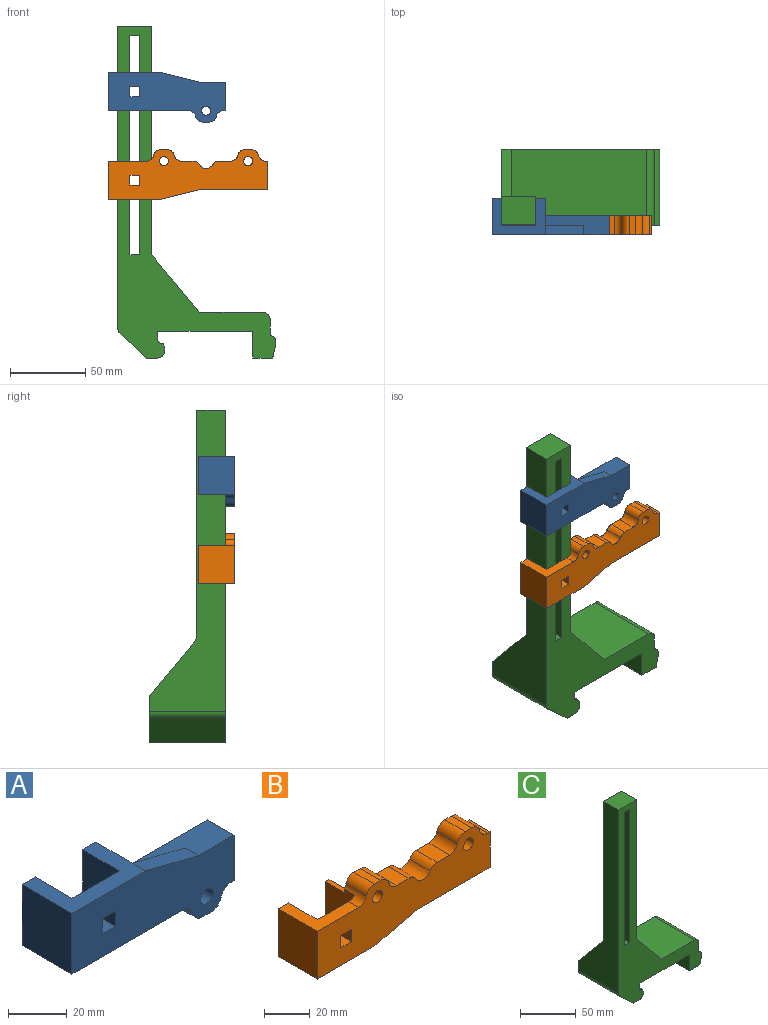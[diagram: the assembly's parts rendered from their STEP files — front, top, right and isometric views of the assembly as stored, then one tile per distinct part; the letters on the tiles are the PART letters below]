
ASSEMBLY  parts=3 mates=2
PART A: 33 faces, bbox 78.2x24.1x33 mm
  f0: plane 25.4x24.13mm, normal (-1,0,0), area 612.9mm2, adj f1,f2,f5,f32
  f1: plane 35.56x24.13mm, normal (0,0,1), area 451.6mm2, adj f0,f5,f6,f7,f8,f9,f16,f31
  f2: plane 53.5x24.13mm, normal (0,0,-1), area 679.4mm2, adj f0,f3,f5,f6,f7,f8,f9,f30
  f3: plane 42.65x26.67mm, normal (0,1,0), area 830.4mm2, adj f2,f4,f9,f14,f15,f18,f19,f20
  f4: plane 12.7x1.29mm, normal (0,0,-1), area 16.3mm2, adj f3,f5,f14,f29
  f5: plane 78.21x33.02mm, normal (0,-1,0), area 1829.8mm2, adj f0,f1,f2,f4,f10,f11,f12,f13
  f6: plane 25.4x22.86mm, normal (0,1,0), area 538.4mm2, adj f1,f2,f7,f8,f10,f11,f12,f13
  f7: plane 25.4x17.78mm, normal (-1,0,0), area 451.6mm2, adj f1,f2,f6,f31
  f8: plane 25.4x17.78mm, normal (1,0,0), area 451.6mm2, adj f1,f2,f6,f32
  f9: plane 25.4x17.78mm, normal (1,0,0), area 330.6mm2, adj f1,f2,f3,f15,f17,f31
  f10: plane 6.5x6.35mm, normal (0,0,1), area 41.3mm2, adj f5,f6,f11,f13
  f11: plane 6.5x6.35mm, normal (-1,0,0), area 41.3mm2, adj f5,f6,f10,f12
  f12: plane 6.5x6.35mm, normal (0,0,-1), area 41.3mm2, adj f5,f6,f11,f13
  f13: plane 6.5x6.35mm, normal (1,0,0), area 41.3mm2, adj f5,f6,f10,f12
  f14: plane 19.05x12.7mm, normal (1,0,0), area 241.9mm2, adj f3,f4,f5,f15
  f15: plane 42.65x12.7mm, normal (0,0,1), area 380.4mm2, adj f3,f5,f9,f14,f16,f17
  f16: plane 25.4x6.35mm, normal (0.24,0,0.97), area 166.3mm2, adj f1,f5,f15,f17
  f17: plane 25.4x6.35mm, normal (0,1,0), area 80.6mm2, adj f9,f15,f16
  f18: plane 12.7x4mm, normal (0,0,-1), area 50.8mm2, adj f3,f5,f19,f20
  f19: cylinder r=5mm len=12.7mm, axis (0,1,0), area 84.5mm2, adj f3,f5,f18,f29
  f20: cylinder r=5mm len=12.7mm, axis (0,-1,0), area 84.5mm2, adj f3,f5,f18,f30
  f21: cylinder r=3.02mm len=8.7mm, axis (0,1,0), area 165.4mm2, adj f5,f28
  f22: plane 5x4mm, normal (0.87,0,0.5), area 23.1mm2, adj f3,f23,f27,f28
  f23: plane 5x4mm, normal (0.87,0,-0.5), area 23.1mm2, adj f3,f22,f24,f28
  f24: plane 5.77x4mm, normal (0,0,-1), area 23.1mm2, adj f3,f23,f25,f28
  f25: plane 5x4mm, normal (-0.87,0,-0.5), area 23.1mm2, adj f3,f24,f26,f28
  f26: plane 5x4mm, normal (-0.87,0,0.5), area 23.1mm2, adj f3,f25,f27,f28
  f27: plane 5.77x4mm, normal (0,0,1), area 23.1mm2, adj f3,f22,f26,f28
  f28: plane 11.55x10mm, normal (0,1,0), area 57.9mm2, adj f21,f22,f23,f24,f25,f26,f27
  f29: cylinder r=5mm len=12.7mm, axis (0,1,0), area 84.5mm2, adj f3,f4,f5,f19
  f30: cylinder r=5mm len=12.7mm, axis (0,-1,0), area 84.5mm2, adj f2,f3,f5,f20
  f31: plane 25.4x6.35mm, normal (0,1,0), area 161.3mm2, adj f1,f2,f7,f9
  f32: plane 25.4x6.35mm, normal (0,1,0), area 161.3mm2, adj f0,f1,f2,f8
PART B: 59 faces, bbox 106.4x24.1x33 mm
  f0: plane 25.4x6.35mm, normal (0,1,0), area 147.5mm2, adj f2,f3,f18,f23,f56,f57
  f1: plane 77.2x26.67mm, normal (0,1,0), area 1352.3mm2, adj f2,f3,f13,f14,f15,f18,f22,f28
  f2: plane 11.43x2.17mm, normal (0,0,1), area 24.8mm2, adj f0,f1,f18,f57
  f3: plane 20.35x17.78mm, normal (1,0,0), area 272.9mm2, adj f0,f1,f15,f23,f30,f56
  f4: plane 5x3.43mm, normal (0.87,0,0.5), area 19.8mm2, adj f5,f9,f40,f58
  f5: plane 5x3.43mm, normal (0.87,0,-0.5), area 19.8mm2, adj f4,f6,f40,f58
  f6: plane 5.77x3.43mm, normal (0,0,-1), area 19.8mm2, adj f5,f7,f40,f58
  f7: plane 5x3.43mm, normal (-0.87,0,-0.5), area 19.8mm2, adj f6,f8,f40,f58
  f8: plane 5x3.43mm, normal (-0.87,0,0.5), area 19.8mm2, adj f7,f9,f40,f58
  f9: plane 5.77x3.43mm, normal (0,0,1), area 19.8mm2, adj f4,f8,f40,f58
  f10: plane 25.5x24.13mm, normal (0,0,1), area 274.8mm2, adj f16,f17,f19,f20,f21,f51
  f11: cylinder r=3.02mm len=8.7mm, axis (0,-1,0), area 165.4mm2, adj f16,f41
  f12: cylinder r=3.02mm len=8.7mm, axis (0,-1,0), area 165.4mm2, adj f16,f40
  f13: plane 12.7x7.63mm, normal (0,0,1), area 96.9mm2, adj f1,f16,f38,f50
  f14: plane 12.7x7.63mm, normal (0,0,1), area 96.9mm2, adj f1,f16,f39,f49
  f15: plane 70.85x12.7mm, normal (0,0,-1), area 738.5mm2, adj f1,f3,f16,f28,f29,f30
  f16: plane 106.41x33.02mm, normal (0,-1,0), area 2399.5mm2, adj f10,f11,f12,f13,f14,f15,f21,f22
  f17: plane 27.05x22.86mm, normal (0,1,0), area 540.3mm2, adj f10,f18,f19,f23,f24,f25,f26,f27
  f18: plane 27.05x17.78mm, normal (-1,0,0), area 462.1mm2, adj f0,f1,f2,f17,f23,f51
  f19: plane 25.4x17.78mm, normal (1,0,0), area 451.6mm2, adj f10,f17,f20,f23
  f20: plane 25.4x6.35mm, normal (0,1,0), area 161.3mm2, adj f10,f19,f21,f23
  f21: plane 25.4x24.13mm, normal (-1,0,0), area 612.9mm2, adj f10,f16,f20,f23
  f22: plane 12.7x1.49mm, normal (0,0,1), area 18.9mm2, adj f1,f16,f28,f48
  f23: plane 35.56x24.13mm, normal (0,0,-1), area 451.6mm2, adj f0,f3,f16,f17,f18,f19,f20,f21
  f24: plane 6.5x6.35mm, normal (0,0,1), area 41.3mm2, adj f16,f17,f25,f27
  f25: plane 6.5x6.35mm, normal (-1,0,0), area 41.3mm2, adj f16,f17,f24,f26
  f26: plane 6.5x6.35mm, normal (0,0,-1), area 41.3mm2, adj f16,f17,f25,f27
  f27: plane 6.5x6.35mm, normal (1,0,0), area 41.3mm2, adj f16,f17,f24,f26
  f28: plane 19.05x12.7mm, normal (1,0,0), area 241.9mm2, adj f1,f15,f16,f22
  f29: plane 25.4x6.35mm, normal (0.24,0,-0.97), area 166.3mm2, adj f15,f16,f23,f30
  f30: plane 25.4x6.35mm, normal (0,1,0), area 80.6mm2, adj f3,f15,f29
  f31: plane 12.7x4mm, normal (0,0,1), area 50.8mm2, adj f1,f16,f35,f36
  f32: plane 12.7x4mm, normal (0,0,1), area 50.8mm2, adj f1,f16,f33,f34
  f33: cylinder r=5mm len=12.7mm, axis (0,-1,0), area 84.5mm2, adj f1,f16,f32,f48
  f34: cylinder r=5mm len=12.7mm, axis (0,1,0), area 84.5mm2, adj f1,f16,f32,f49
  f35: cylinder r=5mm len=12.7mm, axis (0,-1,0), area 84.5mm2, adj f1,f16,f31,f50
  f36: cylinder r=5mm len=12.7mm, axis (0,1,0), area 84.5mm2, adj f1,f16,f31,f51
  f37: cylinder r=5mm len=12.7mm, axis (0,-1,0), area 133mm2, adj f1,f16,f38,f39
  f38: cylinder r=5mm len=12.7mm, axis (0,-1,0), area 66.5mm2, adj f1,f13,f16,f37
  f39: cylinder r=5mm len=12.7mm, axis (0,-1,0), area 66.5mm2, adj f1,f14,f16,f37
  f40: plane 11.55x10mm, normal (0,1,0), area 57.9mm2, adj f4,f5,f6,f7,f8,f9,f12
  f41: plane 11.55x10mm, normal (0,1,0), area 57.9mm2, adj f11,f42,f43,f44,f45,f46,f47
  f42: plane 5x4mm, normal (0.87,0,-0.5), area 23.1mm2, adj f1,f41,f43,f47
  f43: plane 5.77x4mm, normal (0,0,-1), area 23.1mm2, adj f1,f41,f42,f44
  f44: plane 5x4mm, normal (-0.87,0,-0.5), area 23.1mm2, adj f1,f41,f43,f45
  f45: plane 5x4mm, normal (-0.87,0,0.5), area 23.1mm2, adj f1,f41,f44,f46
  f46: plane 5.77x4mm, normal (0,0,1), area 23.1mm2, adj f1,f41,f45,f47
  f47: plane 5x4mm, normal (0.87,0,0.5), area 23.1mm2, adj f1,f41,f42,f46
  f48: cylinder r=5mm len=12.7mm, axis (0,-1,0), area 84.5mm2, adj f1,f16,f22,f33
  f49: cylinder r=5mm len=12.7mm, axis (0,1,0), area 84.5mm2, adj f1,f14,f16,f34
  f50: cylinder r=5mm len=12.7mm, axis (0,-1,0), area 84.5mm2, adj f1,f13,f16,f35
  f51: cylinder r=5mm len=12.7mm, axis (0,1,0), area 57.9mm2, adj f1,f10,f16,f17,f18,f36
  f52: plane 5.83x0.57mm, normal (0,0,-1), area 3.3mm2, adj f1,f53,f55,f58
  f53: plane 5.05x2.92mm, normal (-0.87,0,-0.5), area 3.3mm2, adj f1,f52,f54,f58
  f54: plane 5.05x2.92mm, normal (-0.87,0,0.5), area 3.3mm2, adj f1,f53,f56,f58
  f55: plane 5.05x2.92mm, normal (0.87,0,-0.5), area 3.3mm2, adj f1,f52,f57,f58
  f56: plane 12x5.83mm, normal (0,0,1), area 17.8mm2, adj f0,f1,f3,f54,f57,f58
  f57: plane 12x5.05mm, normal (0.87,0,0.5), area 70mm2, adj f0,f2,f55,f56,f58
  f58: plane 11.66x10.1mm, normal (0,1,0), area 1.7mm2, adj f4,f5,f6,f7,f8,f9,f52,f53
PART C: 43 faces, bbox 105.4x50.8x221 mm
  f0: plane 50.8x1.35mm, normal (1,0,0), area 67.2mm2, adj f2,f3,f4,f27,f35,f36,f37
  f1: plane 50.8x17.76mm, normal (-1,0,0), area 811.5mm2, adj f2,f3,f10,f29,f30,f31,f32,f33
  f2: plane 220.96x105.36mm, normal (0,-1,0), area 5908.5mm2, adj f0,f1,f4,f5,f7,f8,f9,f10
  f3: plane 105.36x30.46mm, normal (0,1,0), area 1876.3mm2, adj f0,f1,f4,f5,f7,f9,f10,f11
  f4: plane 50.8x9.25mm, normal (0.97,0,-0.24), area 442.9mm2, adj f0,f2,f3,f35,f36,f37,f38,f41
  f5: plane 50.8x10.16mm, normal (1,0,0), area 516.1mm2, adj f2,f3,f16,f27
  f6: plane 190.5x22.86mm, normal (0,1,0), area 3185.5mm2, adj f7,f8,f9,f18,f19,f20,f23,f24
  f7: plane 90.17x50.8mm, normal (0,0,1), area 4064.5mm2, adj f2,f3,f6,f8,f16,f20,f21,f22
  f8: plane 190.5x19.05mm, normal (1,0,0), area 3387.1mm2, adj f2,f6,f7,f18,f21,f22
  f9: plane 200.96x50.8mm, normal (-1,0,0), area 4765.2mm2, adj f2,f3,f6,f15,f18,f19
  f10: plane 63.21x50.8mm, normal (0,0,-1), area 3211.3mm2, adj f1,f2,f3,f14
  f11: plane 50.8x2.45mm, normal (0.91,0,0.41), area 136.1mm2, adj f2,f3,f12,f28
  f12: plane 50.8x1.97mm, normal (1,0,0), area 99.8mm2, adj f2,f3,f11,f17
  f13: plane 50.8x17.81mm, normal (-0.67,0,-0.74), area 1224.7mm2, adj f2,f3,f15,f40
  f14: plane 50.8x5.29mm, normal (1,0,0), area 268.7mm2, adj f2,f3,f10,f42
  f15: cylinder r=5.08mm len=50.8mm, axis (0,-1,0), area 214.4mm2, adj f2,f3,f9,f13
  f16: cylinder r=5.08mm len=50.8mm, axis (0,1,0), area 405.4mm2, adj f2,f3,f5,f7
  f17: cylinder r=5.08mm len=50.8mm, axis (0,1,0), area 384.7mm2, adj f2,f3,f12,f40
  f18: plane 22.86x19.05mm, normal (0,0,1), area 435.5mm2, adj f2,f6,f8,f9
  f19: plane 38.1x31.75mm, normal (0,0.77,0.64), area 314.9mm2, adj f3,f6,f9,f20
  f20: plane 38.1x31.75mm, normal (1,0,0), area 604.8mm2, adj f6,f7,f19
  f21: plane 38.1x31.75mm, normal (0.77,0,0.64), area 314.9mm2, adj f2,f7,f8,f22
  f22: plane 38.1x31.75mm, normal (0,1,0), area 604.8mm2, adj f7,f8,f21
  f23: plane 19.05x6.35mm, normal (0,0,1), area 121mm2, adj f2,f6,f24,f26
  f24: plane 146.05x19.05mm, normal (1,0,0), area 2782.3mm2, adj f2,f6,f23,f25
  f25: plane 19.05x6.35mm, normal (0,0,-1), area 121mm2, adj f2,f6,f24,f26
  f26: plane 146.05x19.05mm, normal (-1,0,0), area 2782.3mm2, adj f2,f6,f23,f25
  f27: cylinder r=5mm len=50.8mm, axis (0,-1,0), area 335.2mm2, adj f0,f2,f3,f5
  f28: plane 50.8x0.7mm, normal (0,0,1), area 35.6mm2, adj f2,f3,f11,f42
  f29: plane 6.77x6.55mm, normal (-0.12,-0.87,-0.49), area 37mm2, adj f1,f30,f32,f39
  f30: plane 6.77x5.83mm, normal (-0.24,0,-0.97), area 40.6mm2, adj f1,f29,f31,f39
  f31: plane 6.77x6.55mm, normal (-0.12,0.87,-0.49), area 37mm2, adj f1,f30,f33,f39
  f32: plane 6.26x5.57mm, normal (0.12,-0.87,0.49), area 29.9mm2, adj f1,f29,f34,f39
  f33: plane 6.26x5.57mm, normal (0.12,0.87,0.49), area 29.9mm2, adj f1,f31,f34,f39
  f34: plane 5.83x4.38mm, normal (0.24,0,0.97), area 26.3mm2, adj f1,f32,f33,f39
  f35: plane 0.23x0.13mm, normal (0.12,0.87,0.49), area 0mm2, adj f0,f4,f36
  f36: plane 5.83x0.05mm, normal (0.24,0,0.97), area 0.3mm2, adj f0,f4,f35,f37
  f37: plane 0.23x0.13mm, normal (0.12,-0.87,0.49), area 0mm2, adj f0,f4,f36
  f38: cylinder r=3.12mm len=10.22mm, axis (0.97,0,-0.24), area 176.7mm2, adj f4,f39
  f39: plane 11.66x9.81mm, normal (-0.97,0,0.24), area 57.7mm2, adj f29,f30,f31,f32,f33,f34,f38
  f40: plane 50.8x7.34mm, normal (0,0,-1), area 373.1mm2, adj f2,f3,f13,f17
  f41: plane 50.8x13.26mm, normal (0,0,-1), area 673.5mm2, adj f1,f2,f3,f4
  f42: cylinder r=3mm len=50.8mm, axis (0,1,0), area 239.4mm2, adj f2,f3,f14,f28
PLACE A t=(90.11,-29.28,-47.26)mm
PLACE B t=(90.11,-29.28,-106.16)mm
PLACE C t=(129.48,-13.66,-209.3)mm
MATE slider A.f1 <-> C.f18  axis (0,0,1) through (78.68,-39.06,-34.56)mm
MATE slider C.f18 <-> B.f10  axis (0,0,1) through (78.68,-39.06,-3.56)mm
